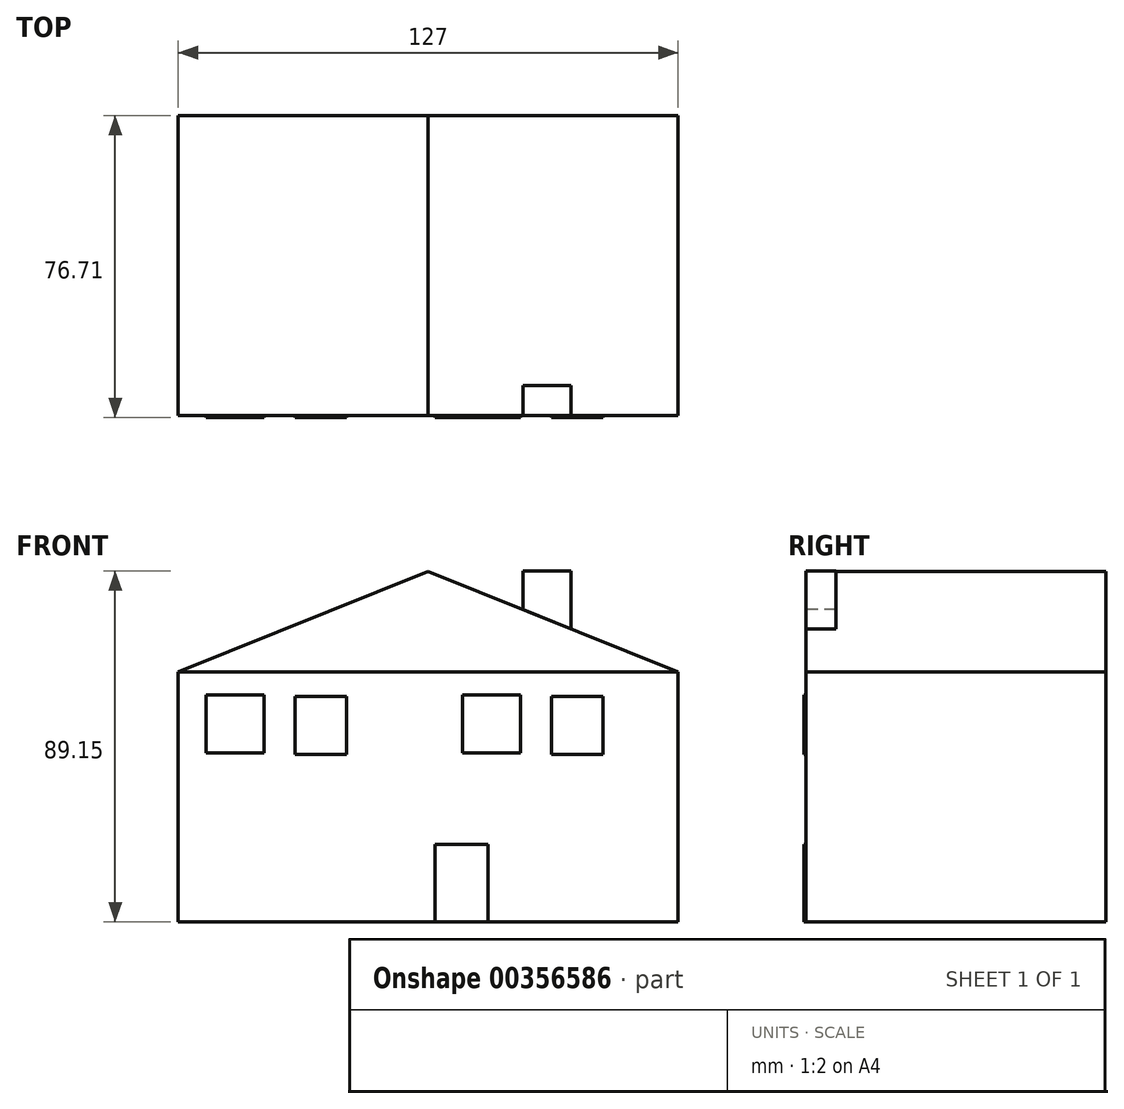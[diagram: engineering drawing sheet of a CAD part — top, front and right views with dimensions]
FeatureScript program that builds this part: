
annotation { "Feature Type Name" : "Feature", "Feature Type Description" : "" }
export const myFeature = defineFeature(function(context is Context, id is Id, definition is map)
    precondition{}
    {
        {
            var Q0;
            Q0=qCreatedBy(makeId("Front.planeOp"),FACE);
            var sketch = newSketch(context, id + "F0", { "sketchPlane" : qUnion([Q0])});
            skLineSegment(sketch, "E0.bottom", {"start": v(-57.58, 49.98) * mm, "end": v(69.42, 49.98) * mm});
            skLineSegment(sketch, "E0.top", {"start": v(-57.58, -13.52) * mm, "end": v(69.42, -13.52) * mm});
            skLineSegment(sketch, "E0.left", {"start": v(-57.58, 49.98) * mm, "end": v(-57.58, -13.52) * mm});
            skLineSegment(sketch, "E0.right", {"start": v(69.42, 49.98) * mm, "end": v(69.42, -13.52) * mm});
            skSolve(sketch);
        }
        {
            var Q0;
            Q0=makeQuery(id+"F0.imprint","IMPRINT",FACE,{"disambiguationData":[TD([[makeQuery(id+"F0.imprint","IMPRINT",EDGE,{"derivedFrom":sQuery(id+"F0.wireOp",EDGE,"E0.bottom")}),-1.0]])]});
            extrude(context, id + "F1", {"entities" : qUnion([Q0]), "depth" : 76.2 * mm});
        }
        {
            var Q0;
            Q0=makeQuery(id+"F1.opExtrude","CAP_FACE",FACE,{"disambiguationData":[OSD([sQuery(id+"F0.wireOp",EDGE,"E0.bottom"),sQuery(id+"F0.wireOp",EDGE,"E0.top"),sQuery(id+"F0.wireOp",EDGE,"E0.left"),sQuery(id+"F0.wireOp",EDGE,"E0.right")])],"isStart":false});
            var sketch = newSketch(context, id + "F2", { "sketchPlane" : qUnion([Q0])});
            skLineSegment(sketch, "E1.bottom", {"start": v(7.71, 6.21) * mm, "end": v(21.1, 6.21) * mm});
            skLineSegment(sketch, "E1.top", {"start": v(7.71, -13.52) * mm, "end": v(21.1, -13.52) * mm});
            skLineSegment(sketch, "E1.left", {"start": v(7.71, 6.21) * mm, "end": v(7.71, -13.52) * mm});
            skLineSegment(sketch, "E1.right", {"start": v(21.1, 6.21) * mm, "end": v(21.1, -13.52) * mm});
            skLineSegment(sketch, "E2.bottom", {"start": v(-50.45, 44.12) * mm, "end": v(-35.75, 44.12) * mm});
            skLineSegment(sketch, "E2.top", {"start": v(-50.45, 29.41) * mm, "end": v(-35.75, 29.41) * mm});
            skLineSegment(sketch, "E2.left", {"start": v(-50.45, 44.12) * mm, "end": v(-50.45, 29.41) * mm});
            skLineSegment(sketch, "E2.right", {"start": v(-35.75, 44.12) * mm, "end": v(-35.75, 29.41) * mm});
            skLineSegment(sketch, "E3.bottom", {"start": v(-27.9, 43.79) * mm, "end": v(-14.83, 43.79) * mm});
            skLineSegment(sketch, "E3.top", {"start": v(-27.9, 29.08) * mm, "end": v(-14.83, 29.08) * mm});
            skLineSegment(sketch, "E3.left", {"start": v(-27.9, 43.79) * mm, "end": v(-27.9, 29.08) * mm});
            skLineSegment(sketch, "E3.right", {"start": v(-14.83, 43.79) * mm, "end": v(-14.83, 29.08) * mm});
            skLineSegment(sketch, "E4.bottom", {"start": v(14.66, 44.12) * mm, "end": v(29.36, 44.12) * mm});
            skLineSegment(sketch, "E4.top", {"start": v(14.66, 29.41) * mm, "end": v(29.36, 29.41) * mm});
            skLineSegment(sketch, "E4.left", {"start": v(14.66, 44.12) * mm, "end": v(14.66, 29.41) * mm});
            skLineSegment(sketch, "E4.right", {"start": v(29.36, 44.12) * mm, "end": v(29.36, 29.41) * mm});
            skLineSegment(sketch, "E5.bottom", {"start": v(37.2, 43.79) * mm, "end": v(50.27, 43.79) * mm});
            skLineSegment(sketch, "E5.top", {"start": v(37.2, 29.08) * mm, "end": v(50.27, 29.08) * mm});
            skLineSegment(sketch, "E5.left", {"start": v(37.2, 43.79) * mm, "end": v(37.2, 29.08) * mm});
            skLineSegment(sketch, "E5.right", {"start": v(50.27, 43.79) * mm, "end": v(50.27, 29.08) * mm});
            skSolve(sketch);
        }
        {
            var Q0;
            Q0 = qSketchRegion(id + "F2", true);
            extrude(context, id + "F3", {"entities" : qUnion([Q0]), "operationType" : NewBodyOperationType.ADD, "depth" : 0.5 * mm});
        }
        {
            var Q0;
            Q0=makeQuery(id+"F1.opExtrude","CAP_FACE",FACE,{"disambiguationData":[OSD([sQuery(id+"F0.wireOp",EDGE,"E0.bottom"),sQuery(id+"F0.wireOp",EDGE,"E0.top"),sQuery(id+"F0.wireOp",EDGE,"E0.left"),sQuery(id+"F0.wireOp",EDGE,"E0.right")])],"isStart":false});
            var sketch = newSketch(context, id + "F4", { "sketchPlane" : qUnion([Q0])});
            skLineSegment(sketch, "E6", {"start": v(5.92, 49.98) * mm, "end": v(5.92, 75.48) * mm, "construction": true});
            skPoint(sketch, "E6.endSnap0", {"position": v(5.92, 49.98) * mm});
            skLineSegment(sketch, "E7", {"start": v(5.92, 75.48) * mm, "end": v(-57.58, 49.98) * mm});
            skLineSegment(sketch, "E8", {"start": v(5.92, 75.48) * mm, "end": v(69.42, 49.98) * mm});
            skSolve(sketch);
        }
        {
            var Q0;
            Q0=makeQuery(id+"F4.imprint","IMPRINT",FACE,{"disambiguationData":[TD([[makeQuery(id+"F4.imprint","IMPRINT",EDGE,{"derivedFrom":sQuery(id+"F4.wireOp",EDGE,"E7")}),1.0]])]});
            extrude(context, id + "F5", {"entities" : qUnion([Q0]), "oppositeDirection" : true, "depth" : 76.2 * mm});
        }
        {
            var Q0;
            Q0=makeQuery(id+"F5.opExtrude","CAP_FACE",FACE,{"disambiguationData":[OSD([sQuery(id+"F0.wireOp",EDGE,"E0.bottom"),sQuery(id+"F4.wireOp",EDGE,"E7"),sQuery(id+"F4.wireOp",EDGE,"E8")])],"isStart":true});
            var sketch = newSketch(context, id + "F6", { "sketchPlane" : qUnion([Q0])});
            skLineSegment(sketch, "E9", {"start": v(29.98, 65.82) * mm, "end": v(29.98, 75.63) * mm});
            skLineSegment(sketch, "E10", {"start": v(29.98, 75.63) * mm, "end": v(42.15, 75.63) * mm});
            skLineSegment(sketch, "E11", {"start": v(42.15, 75.63) * mm, "end": v(42.15, 60.93) * mm});
            skSolve(sketch);
        }
        {
            var Q0;
            {var subQ0=sQuery(id+"F6.wireOp",EDGE,"E9");Q0=makeQuery(id+"F6.imprint","IMPRINT",FACE,{"disambiguationData":[TD([[makeQuery(id+"F6.imprint","IMPRINT",EDGE,{"derivedFrom":subQ0}),-1.0]])]});}
            extrude(context, id + "F7", {"entities" : qUnion([Q0]), "oppositeDirection" : true, "depth" : 7.62 * mm});
        }
    });
